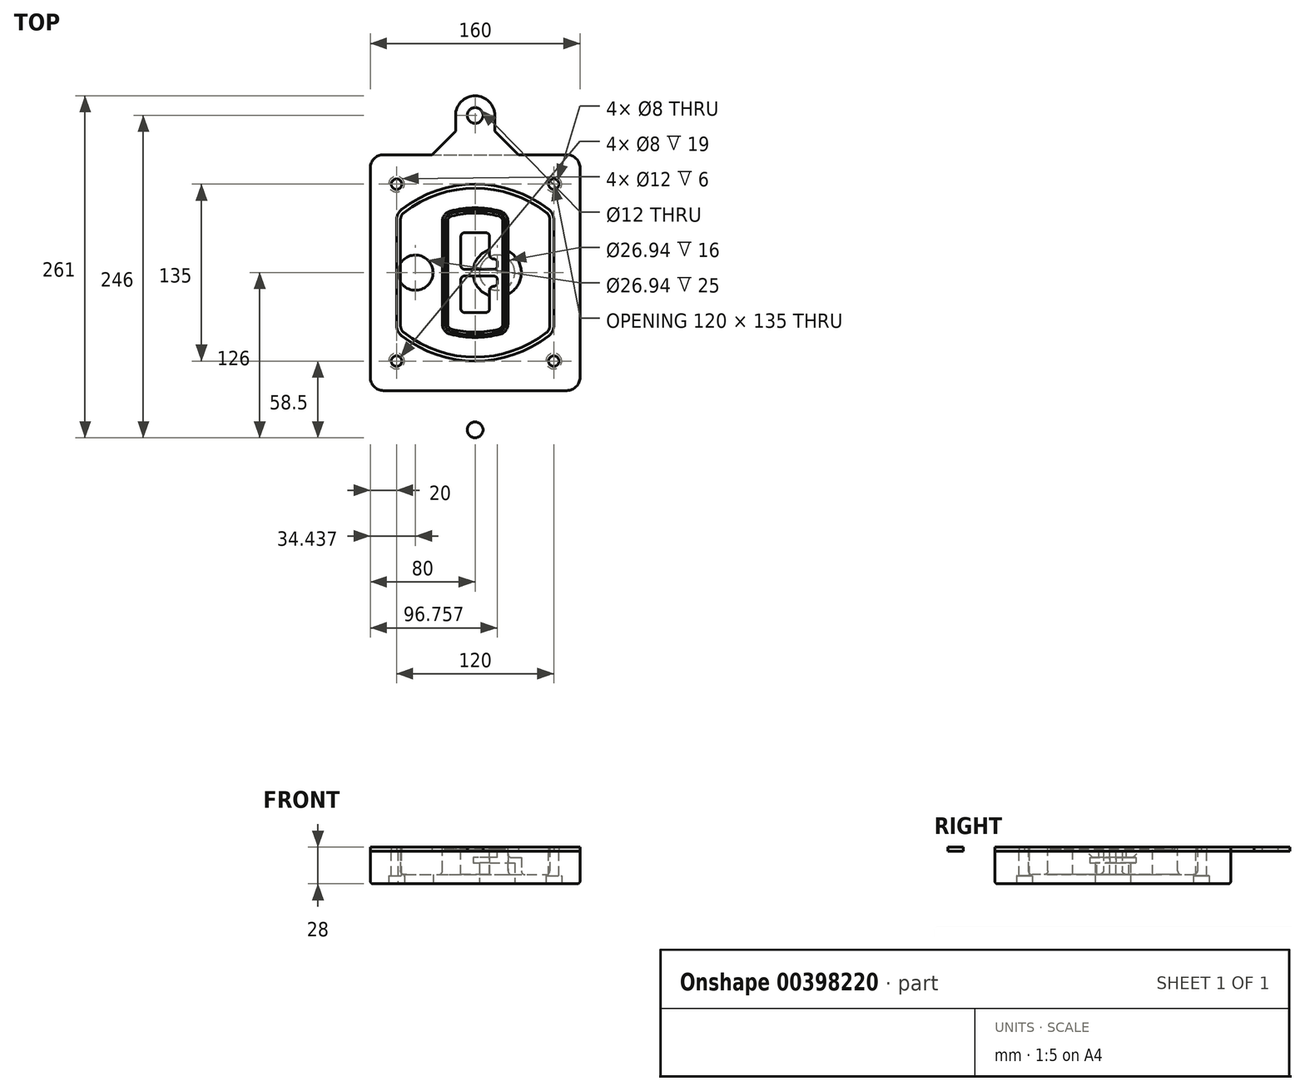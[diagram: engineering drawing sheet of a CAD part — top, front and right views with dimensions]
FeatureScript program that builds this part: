
annotation { "Feature Type Name" : "Feature", "Feature Type Description" : "" }
export const myFeature = defineFeature(function(context is Context, id is Id, definition is map)
    precondition{}
    {
        {
            var Q0;
            Q0=qCreatedBy(makeId("Top.planeOp"),FACE);
            var sketch = newSketch(context, id + "F0", { "sketchPlane" : qUnion([Q0])});
            skPoint(sketch, "E0.rect.middle", {"position": v(0, 0) * mm});
            skLineSegment(sketch, "E1.bottom", {"start": v(-70, -90) * mm, "end": v(70, -90) * mm});
            skLineSegment(sketch, "E1.top", {"start": v(-70, 90) * mm, "end": v(70, 90) * mm});
            skLineSegment(sketch, "E1.left", {"start": v(-80, -80) * mm, "end": v(-80, 80) * mm});
            skLineSegment(sketch, "E1.right", {"start": v(80, -80) * mm, "end": v(80, 80) * mm});
            skLineSegment(sketch, "E2", {"start": v(-80, 90) * mm, "end": v(80, -90) * mm, "construction": true});
            skLineSegment(sketch, "E3", {"start": v(80, 90) * mm, "end": v(-80, -90) * mm, "construction": true});
            skCircle(sketch, "E4", {"center": v(-60, 67.5) * mm, "radius": 4 * mm});
            skCircle(sketch, "E5", {"center": v(60, 67.5) * mm, "radius": 4 * mm});
            skCircle(sketch, "E6", {"center": v(60, -67.5) * mm, "radius": 4 * mm});
            skCircle(sketch, "E7", {"center": v(-60, -67.5) * mm, "radius": 4 * mm});
            skLineSegment(sketch, "E8", {"start": v(-60, 67.5) * mm, "end": v(60, 67.5) * mm, "construction": true});
            skLineSegment(sketch, "E9", {"start": v(60, 67.5) * mm, "end": v(60, -67.5) * mm, "construction": true});
            skLineSegment(sketch, "E10", {"start": v(60, -67.5) * mm, "end": v(-60, -67.5) * mm, "construction": true});
            skLineSegment(sketch, "E11", {"start": v(-60, -67.5) * mm, "end": v(-60, 67.5) * mm, "construction": true});
            skLineSegment(sketch, "E12", {"start": v(-60, 40.3) * mm, "end": v(-60, -40.3) * mm});
            skLineSegment(sketch, "E13", {"start": v(60, 40.3) * mm, "end": v(60, -40.3) * mm});
            skArc(sketch, "E14", {"start": v(56.15, 48.18) * mm, "mid": v(0, 67.5) * mm, "end": v(-56.15, 48.18) * mm});
            skArc(sketch, "E15", {"start": v(-56.15, -48.18) * mm, "mid": v(0, -67.5) * mm, "end": v(56.15, -48.18) * mm});
            skLineSegment(sketch, "E16", {"start": v(-60, 0) * mm, "end": v(60, 0) * mm, "construction": true});
            skPoint(sketch, "E17.visualSharp", {"position": v(-60, -45) * mm});
            skArc(sketch, "E17.filletArc", {"start": v(-60, -40.3) * mm, "mid": v(-58.99, -44.68) * mm, "end": v(-56.15, -48.18) * mm});
            skPoint(sketch, "E18.visualSharp", {"position": v(-60, 45) * mm});
            skArc(sketch, "E18.filletArc", {"start": v(-56.15, 48.18) * mm, "mid": v(-58.99, 44.68) * mm, "end": v(-60, 40.3) * mm});
            skPoint(sketch, "E19.visualSharp", {"position": v(60, 45) * mm});
            skArc(sketch, "E19.filletArc", {"start": v(60, 40.3) * mm, "mid": v(58.99, 44.68) * mm, "end": v(56.15, 48.18) * mm});
            skPoint(sketch, "E20.visualSharp", {"position": v(60, -45) * mm});
            skArc(sketch, "E20.filletArc", {"start": v(56.15, -48.18) * mm, "mid": v(58.99, -44.68) * mm, "end": v(60, -40.3) * mm});
            skPoint(sketch, "E21.visualSharp", {"position": v(-80, 90) * mm});
            skArc(sketch, "E21.filletArc", {"start": v(-70, 90) * mm, "mid": v(-77.07, 87.07) * mm, "end": v(-80, 80) * mm});
            skPoint(sketch, "E22.visualSharp", {"position": v(80, 90) * mm});
            skArc(sketch, "E22.filletArc", {"start": v(80, 80) * mm, "mid": v(77.07, 87.07) * mm, "end": v(70, 90) * mm});
            skPoint(sketch, "E23.visualSharp", {"position": v(80, -90) * mm});
            skArc(sketch, "E23.filletArc", {"start": v(70, -90) * mm, "mid": v(77.07, -87.07) * mm, "end": v(80, -80) * mm});
            skPoint(sketch, "E24.visualSharp", {"position": v(-80, -90) * mm});
            skArc(sketch, "E24.filletArc", {"start": v(-80, -80) * mm, "mid": v(-77.07, -87.07) * mm, "end": v(-70, -90) * mm});
            skArc(sketch, "E25.0", {"start": v(57, 40.3) * mm, "mid": v(56.3, 43.36) * mm, "end": v(54.3, 45.81) * mm});
            skLineSegment(sketch, "E25.1", {"start": v(57, 40.3) * mm, "end": v(57, -40.3) * mm});
            skArc(sketch, "E25.2", {"start": v(54.3, -45.81) * mm, "mid": v(56.3, -43.36) * mm, "end": v(57, -40.3) * mm});
            skArc(sketch, "E25.3", {"start": v(-54.3, -45.81) * mm, "mid": v(0, -64.5) * mm, "end": v(54.3, -45.81) * mm});
            skArc(sketch, "E25.4", {"start": v(-57, -40.3) * mm, "mid": v(-56.3, -43.36) * mm, "end": v(-54.3, -45.81) * mm});
            skArc(sketch, "E25.5", {"start": v(54.3, 45.81) * mm, "mid": v(0, 64.5) * mm, "end": v(-54.3, 45.81) * mm});
            skLineSegment(sketch, "E25.6", {"start": v(-57, 40.3) * mm, "end": v(-57, -40.3) * mm});
            skArc(sketch, "E25.7", {"start": v(-54.3, 45.81) * mm, "mid": v(-56.3, 43.36) * mm, "end": v(-57, 40.3) * mm});
            skArc(sketch, "E26.0", {"start": v(-58.62, 51.33) * mm, "mid": v(-62.58, 46.43) * mm, "end": v(-64, 40.3) * mm});
            skArc(sketch, "E26.1", {"start": v(58.62, 51.33) * mm, "mid": v(0, 71.5) * mm, "end": v(-58.62, 51.33) * mm});
            skArc(sketch, "E26.2", {"start": v(64, 40.3) * mm, "mid": v(62.58, 46.43) * mm, "end": v(58.62, 51.33) * mm});
            skLineSegment(sketch, "E26.3", {"start": v(64, 40.3) * mm, "end": v(64, -40.3) * mm});
            skArc(sketch, "E26.4", {"start": v(58.62, -51.33) * mm, "mid": v(62.58, -46.43) * mm, "end": v(64, -40.3) * mm});
            skLineSegment(sketch, "E26.5", {"start": v(-64, 40.3) * mm, "end": v(-64, -40.3) * mm});
            skArc(sketch, "E26.6", {"start": v(-58.62, -51.33) * mm, "mid": v(0, -71.5) * mm, "end": v(58.62, -51.33) * mm});
            skArc(sketch, "E26.7", {"start": v(-64, -40.3) * mm, "mid": v(-62.58, -46.43) * mm, "end": v(-58.62, -51.33) * mm});
            skSolve(sketch);
        }
        {
            var Q0;
            Q0=makeQuery(id+"F0.imprint","IMPRINT",FACE,{"disambiguationData":[TD([[makeQuery(id+"F0.imprint","IMPRINT",EDGE,{"derivedFrom":sQuery(id+"F0.wireOp",EDGE,"E1.bottom")}),1.0]])]});
            var Q1;
            Q1=makeQuery(id+"F0.imprint","IMPRINT",FACE,{"disambiguationData":[TD([[makeQuery(id+"F0.imprint","IMPRINT",EDGE,{"derivedFrom":sQuery(id+"F0.wireOp",EDGE,"E12")}),1.0]])]});
            var Q2;
            Q2=makeQuery(id+"F0.imprint","IMPRINT",FACE,{"disambiguationData":[TD([[makeQuery(id+"F0.imprint","IMPRINT",EDGE,{"derivedFrom":sQuery(id+"F0.wireOp",EDGE,"E25.0")}),1.0]])]});
            var Q3;
            Q3=makeQuery(id+"F0.imprint","IMPRINT",FACE,{"disambiguationData":[TD([[makeQuery(id+"F0.imprint","IMPRINT",EDGE,{"derivedFrom":sQuery(id+"F0.wireOp",EDGE,"E12")}),-1.0]])]});
            extrude(context, id + "F1", {"entities" : qUnion([Q0, Q1, Q2, Q3]), "oppositeDirection" : true, "depth" : 25 * mm});
        }
        {
            var Q0;
            Q0=makeQuery(id+"F0.imprint","IMPRINT",FACE,{"disambiguationData":[TD([[makeQuery(id+"F0.imprint","IMPRINT",EDGE,{"derivedFrom":sQuery(id+"F0.wireOp",EDGE,"E12")}),1.0]])]});
            extrude(context, id + "F2", {"entities" : qUnion([Q0]), "operationType" : NewBodyOperationType.ADD, "depth" : 3 * mm});
        }
        {
            var Q0;
            Q0=makeQuery(id+"F0.imprint","IMPRINT",FACE,{"disambiguationData":[TD([[makeQuery(id+"F0.imprint","IMPRINT",EDGE,{"derivedFrom":sQuery(id+"F0.wireOp",EDGE,"E25.0")}),1.0]])]});
            extrude(context, id + "F3", {"entities" : qUnion([Q0]), "operationType" : NewBodyOperationType.REMOVE, "oppositeDirection" : true, "depth" : 18 * mm});
        }
        {
            var Q0;
            Q0=makeQuery(id+"F2.opExtrude","CAP_FACE",FACE,{"disambiguationData":[OSD([sQuery(id+"F0.wireOp",EDGE,"E12"),sQuery(id+"F0.wireOp",EDGE,"E13"),sQuery(id+"F0.wireOp",EDGE,"E14"),sQuery(id+"F0.wireOp",EDGE,"E15"),sQuery(id+"F0.wireOp",EDGE,"E17.filletArc"),sQuery(id+"F0.wireOp",EDGE,"E18.filletArc"),sQuery(id+"F0.wireOp",EDGE,"E19.filletArc"),sQuery(id+"F0.wireOp",EDGE,"E20.filletArc"),sQuery(id+"F0.wireOp",EDGE,"E25.0"),sQuery(id+"F0.wireOp",EDGE,"E25.1"),sQuery(id+"F0.wireOp",EDGE,"E25.2"),sQuery(id+"F0.wireOp",EDGE,"E25.3"),sQuery(id+"F0.wireOp",EDGE,"E25.4"),sQuery(id+"F0.wireOp",EDGE,"E25.5"),sQuery(id+"F0.wireOp",EDGE,"E25.6"),sQuery(id+"F0.wireOp",EDGE,"E25.7")])],"isStart":false});
            var sketch = newSketch(context, id + "F4", { "sketchPlane" : qUnion([Q0])});
            skArc(sketch, "E27.0", {"start": v(-19.08, -46.97) * mm, "mid": v(0, -49.5) * mm, "end": v(19.08, -46.97) * mm});
            skArc(sketch, "E28.0", {"start": v(19.08, 46.97) * mm, "mid": v(0, 49.5) * mm, "end": v(-19.08, 46.97) * mm});
            skLineSegment(sketch, "E29", {"start": v(-25, 39.25) * mm, "end": v(-25, -39.25) * mm});
            skLineSegment(sketch, "E30", {"start": v(25, 39.25) * mm, "end": v(25, -39.25) * mm});
            skLineSegment(sketch, "E31", {"start": v(-25, 45.1) * mm, "end": v(25, 45.1) * mm, "construction": true});
            skLineSegment(sketch, "E32", {"start": v(-25, -45.1) * mm, "end": v(25, -45.1) * mm, "construction": true});
            skPoint(sketch, "E33.visualSharp", {"position": v(-25, 45.1) * mm});
            skArc(sketch, "E33.filletArc", {"start": v(-19.08, 46.97) * mm, "mid": v(-23.35, 44.11) * mm, "end": v(-25, 39.25) * mm});
            skPoint(sketch, "E34.visualSharp", {"position": v(25, 45.1) * mm});
            skArc(sketch, "E34.filletArc", {"start": v(25, 39.25) * mm, "mid": v(23.35, 44.11) * mm, "end": v(19.08, 46.97) * mm});
            skPoint(sketch, "E35.visualSharp", {"position": v(25, -45.1) * mm});
            skArc(sketch, "E35.filletArc", {"start": v(19.08, -46.97) * mm, "mid": v(23.35, -44.11) * mm, "end": v(25, -39.25) * mm});
            skPoint(sketch, "E36.visualSharp", {"position": v(-25, -45.1) * mm});
            skArc(sketch, "E36.filletArc", {"start": v(-25, -39.25) * mm, "mid": v(-23.35, -44.11) * mm, "end": v(-19.08, -46.97) * mm});
            skArc(sketch, "E37.0", {"start": v(54.3, 45.81) * mm, "mid": v(0, 64.5) * mm, "end": v(-54.3, 45.81) * mm});
            skArc(sketch, "E37.1", {"start": v(-54.3, 45.81) * mm, "mid": v(-56.3, 43.36) * mm, "end": v(-57, 40.3) * mm});
            skLineSegment(sketch, "E37.2", {"start": v(-57, 40.3) * mm, "end": v(-57, -40.3) * mm});
            skArc(sketch, "E37.3", {"start": v(-57, -40.3) * mm, "mid": v(-56.3, -43.36) * mm, "end": v(-54.3, -45.81) * mm});
            skArc(sketch, "E37.4", {"start": v(-54.3, -45.81) * mm, "mid": v(0, -64.5) * mm, "end": v(54.3, -45.81) * mm});
            skArc(sketch, "E37.5", {"start": v(54.3, -45.81) * mm, "mid": v(56.3, -43.36) * mm, "end": v(57, -40.3) * mm});
            skLineSegment(sketch, "E37.6", {"start": v(57, 40.3) * mm, "end": v(57, -40.3) * mm});
            skArc(sketch, "E37.7", {"start": v(57, 40.3) * mm, "mid": v(56.3, 43.36) * mm, "end": v(54.3, 45.81) * mm});
            skLineSegment(sketch, "E38.0", {"start": v(23, 39.25) * mm, "end": v(23, -39.25) * mm});
            skArc(sketch, "E38.1", {"start": v(18.56, -45.04) * mm, "mid": v(21.76, -42.9) * mm, "end": v(23, -39.25) * mm});
            skArc(sketch, "E38.2", {"start": v(-18.56, -45.04) * mm, "mid": v(0, -47.5) * mm, "end": v(18.56, -45.04) * mm});
            skArc(sketch, "E38.3", {"start": v(-23, -39.25) * mm, "mid": v(-21.76, -42.9) * mm, "end": v(-18.56, -45.04) * mm});
            skLineSegment(sketch, "E38.4", {"start": v(-23, 39.25) * mm, "end": v(-23, -39.25) * mm});
            skArc(sketch, "E38.5", {"start": v(23, 39.25) * mm, "mid": v(21.76, 42.9) * mm, "end": v(18.56, 45.04) * mm});
            skArc(sketch, "E38.6", {"start": v(-18.56, 45.04) * mm, "mid": v(-21.76, 42.9) * mm, "end": v(-23, 39.25) * mm});
            skArc(sketch, "E38.7", {"start": v(18.56, 45.04) * mm, "mid": v(0, 47.5) * mm, "end": v(-18.56, 45.04) * mm});
            skArc(sketch, "E39.0", {"start": v(21, 39.25) * mm, "mid": v(20.18, 41.68) * mm, "end": v(18.04, 43.1) * mm});
            skLineSegment(sketch, "E39.1", {"start": v(21, 39.25) * mm, "end": v(21, -39.25) * mm});
            skArc(sketch, "E39.2", {"start": v(18.04, -43.1) * mm, "mid": v(20.18, -41.68) * mm, "end": v(21, -39.25) * mm});
            skArc(sketch, "E39.3", {"start": v(-18.04, -43.1) * mm, "mid": v(0, -45.5) * mm, "end": v(18.04, -43.1) * mm});
            skArc(sketch, "E39.4", {"start": v(-21, -39.25) * mm, "mid": v(-20.18, -41.68) * mm, "end": v(-18.04, -43.1) * mm});
            skArc(sketch, "E39.5", {"start": v(18.04, 43.1) * mm, "mid": v(0, 45.5) * mm, "end": v(-18.04, 43.1) * mm});
            skLineSegment(sketch, "E39.6", {"start": v(-21, 39.25) * mm, "end": v(-21, -39.25) * mm});
            skArc(sketch, "E39.7", {"start": v(-18.04, 43.1) * mm, "mid": v(-20.18, 41.68) * mm, "end": v(-21, 39.25) * mm});
            skLineSegment(sketch, "E40", {"start": v(-25, 0) * mm, "end": v(25, 0) * mm, "construction": true});
            skLineSegment(sketch, "E41", {"start": v(-11, 5.5) * mm, "end": v(-11, 27.5) * mm});
            skLineSegment(sketch, "E42", {"start": v(-8, 30.5) * mm, "end": v(8, 30.5) * mm});
            skLineSegment(sketch, "E43", {"start": v(11, 27.5) * mm, "end": v(11, 13.5) * mm});
            skLineSegment(sketch, "E44", {"start": v(14, 10.5) * mm, "end": v(14, 10.5) * mm});
            skLineSegment(sketch, "E45", {"start": v(17, 7.5) * mm, "end": v(17, 5.5) * mm});
            skLineSegment(sketch, "E46", {"start": v(14, 2.5) * mm, "end": v(-8, 2.5) * mm});
            skPoint(sketch, "E47.visualSharp", {"position": v(-11, 30.5) * mm});
            skArc(sketch, "E47.filletArc", {"start": v(-8, 30.5) * mm, "mid": v(-10.12, 29.62) * mm, "end": v(-11, 27.5) * mm});
            skPoint(sketch, "E48.visualSharp", {"position": v(11, 30.5) * mm});
            skArc(sketch, "E48.filletArc", {"start": v(11, 27.5) * mm, "mid": v(10.12, 29.62) * mm, "end": v(8, 30.5) * mm});
            skPoint(sketch, "E49.visualSharp", {"position": v(11, 10.5) * mm});
            skArc(sketch, "E49.filletArc", {"start": v(11, 13.5) * mm, "mid": v(11.88, 11.38) * mm, "end": v(14, 10.5) * mm});
            skPoint(sketch, "E50.visualSharp", {"position": v(17, 10.5) * mm});
            skArc(sketch, "E50.filletArc", {"start": v(17, 7.5) * mm, "mid": v(16.12, 9.62) * mm, "end": v(14, 10.5) * mm});
            skPoint(sketch, "E51.visualSharp", {"position": v(17, 2.5) * mm});
            skArc(sketch, "E51.filletArc", {"start": v(14, 2.5) * mm, "mid": v(16.12, 3.38) * mm, "end": v(17, 5.5) * mm});
            skPoint(sketch, "E52.visualSharp", {"position": v(-11, 2.5) * mm});
            skArc(sketch, "E52.filletArc", {"start": v(-11, 5.5) * mm, "mid": v(-10.12, 3.38) * mm, "end": v(-8, 2.5) * mm});
            skLineSegment(sketch, "E53.0.MirrorCS", {"start": v(14, -2.5) * mm, "end": v(-8, -2.5) * mm});
            skArc(sketch, "E54.0.MirrorCS", {"start": v(-11, -5.5) * mm, "mid": v(-10.12, -3.38) * mm, "end": v(-8, -2.5) * mm});
            skLineSegment(sketch, "E55.0.MirrorCS", {"start": v(-11, -5.5) * mm, "end": v(-11, -27.5) * mm});
            skArc(sketch, "E56.0.MirrorCS", {"start": v(-8, -30.5) * mm, "mid": v(-10.12, -29.62) * mm, "end": v(-11, -27.5) * mm});
            skLineSegment(sketch, "E57.0.MirrorCS", {"start": v(-8, -30.5) * mm, "end": v(8, -30.5) * mm});
            skArc(sketch, "E58.0.MirrorCS", {"start": v(11, -27.5) * mm, "mid": v(10.12, -29.62) * mm, "end": v(8, -30.5) * mm});
            skLineSegment(sketch, "E59.0.MirrorCS", {"start": v(11, -27.5) * mm, "end": v(11, -13.5) * mm});
            skArc(sketch, "E60.0.MirrorCS", {"start": v(11, -13.5) * mm, "mid": v(11.88, -11.38) * mm, "end": v(14, -10.5) * mm});
            skArc(sketch, "E61.0.MirrorCS", {"start": v(17, -7.5) * mm, "mid": v(16.12, -9.62) * mm, "end": v(14, -10.5) * mm});
            skLineSegment(sketch, "E62.0.MirrorCS", {"start": v(17, -7.5) * mm, "end": v(17, -5.5) * mm});
            skArc(sketch, "E63.0.MirrorCS", {"start": v(14, -2.5) * mm, "mid": v(16.12, -3.38) * mm, "end": v(17, -5.5) * mm});
            skSolve(sketch);
        }
        {
            var Q0;
            Q0=makeQuery(id+"F4.imprint","IMPRINT",FACE,{"disambiguationData":[TD([[makeQuery(id+"F4.imprint","IMPRINT",EDGE,{"derivedFrom":sQuery(id+"F4.wireOp",EDGE,"E27.0")}),1.0]])]});
            var Q1;
            Q1=makeQuery(id+"F4.imprint","IMPRINT",FACE,{"disambiguationData":[TD([[makeQuery(id+"F4.imprint","IMPRINT",EDGE,{"derivedFrom":sQuery(id+"F4.wireOp",EDGE,"E38.0")}),-1.0]])]});
            var Q2;
            Q2=makeQuery(id+"F4.imprint","IMPRINT",FACE,{"disambiguationData":[TD([[makeQuery(id+"F4.imprint","IMPRINT",EDGE,{"derivedFrom":sQuery(id+"F4.wireOp",EDGE,"E39.0")}),1.0]])]});
            extrude(context, id + "F5", {"entities" : qUnion([Q0, Q1, Q2]), "operationType" : NewBodyOperationType.ADD, "endBound" : BoundingType.UP_TO_NEXT, "oppositeDirection" : true, "depth" : 25 * mm});
        }
        {
            var Q0;
            Q0=makeQuery(id+"F4.imprint","IMPRINT",FACE,{"disambiguationData":[TD([[makeQuery(id+"F4.imprint","IMPRINT",EDGE,{"derivedFrom":sQuery(id+"F4.wireOp",EDGE,"E38.0")}),-1.0]])]});
            extrude(context, id + "F6", {"entities" : qUnion([Q0]), "operationType" : NewBodyOperationType.REMOVE, "oppositeDirection" : true, "depth" : 2 * mm});
        }
        {
            var Q0;
            Q0=makeQuery(id+"F1.opExtrude","CAP_FACE",FACE,{"disambiguationData":[OSD([sQuery(id+"F0.wireOp",EDGE,"E1.bottom"),sQuery(id+"F0.wireOp",EDGE,"E1.top"),sQuery(id+"F0.wireOp",EDGE,"E1.left"),sQuery(id+"F0.wireOp",EDGE,"E1.right"),sQuery(id+"F0.wireOp",EDGE,"E4"),sQuery(id+"F0.wireOp",EDGE,"E5"),sQuery(id+"F0.wireOp",EDGE,"E6"),sQuery(id+"F0.wireOp",EDGE,"E7"),sQuery(id+"F0.wireOp",EDGE,"E21.filletArc"),sQuery(id+"F0.wireOp",EDGE,"E22.filletArc"),sQuery(id+"F0.wireOp",EDGE,"E23.filletArc"),sQuery(id+"F0.wireOp",EDGE,"E24.filletArc")])],"isStart":false});
            var sketch = newSketch(context, id + "F7", { "sketchPlane" : qUnion([Q0])});
            skCircle(sketch, "E64", {"center": v(16.76, 0) * mm, "radius": 13.47 * mm});
            skCircle(sketch, "E65", {"center": v(-45.56, 0) * mm, "radius": 13.47 * mm});
            skLineSegment(sketch, "E66", {"start": v(80, 0) * mm, "end": v(-80, 0) * mm});
            skCircle(sketch, "E67", {"center": v(16.76, 0) * mm, "radius": 18.47 * mm});
            skCircle(sketch, "E68", {"center": v(60, -67.5) * mm, "radius": 6 * mm});
            skCircle(sketch, "E69", {"center": v(-60, -67.5) * mm, "radius": 6 * mm});
            skCircle(sketch, "E70", {"center": v(-60, 67.5) * mm, "radius": 6 * mm});
            skCircle(sketch, "E71", {"center": v(60, 67.5) * mm, "radius": 6 * mm});
            skSolve(sketch);
        }
        {
            var Q0;
            {var subQ1=sQuery(id+"F7.wireOp",EDGE,"E66");var subQ4=sQuery(id+"F7.wireOp",EDGE,"E64");var subQ6=makeQuery(id+"F7.imprint","INTERSECT",VERTEX,{"disambiguationData":[OD(0.0)],"derivedFrom":[subQ4,subQ1]});Q0=makeQuery(id+"F7.imprint","IMPRINT",FACE,{"disambiguationData":[TD([[makeQuery(id+"F7.imprint","IMPRINT",EDGE,{"disambiguationData":[TD([[subQ6,-1.0]])],"derivedFrom":subQ4}),-1.0]])]});}
            var Q1;
            {var subQ0=sQuery(id+"F7.wireOp",EDGE,"E66");var subQ1=sQuery(id+"F7.wireOp",EDGE,"E64");var subQ3=makeQuery(id+"F7.imprint","INTERSECT",VERTEX,{"disambiguationData":[OD(0.0)],"derivedFrom":[subQ1,subQ0]});Q1=makeQuery(id+"F7.imprint","IMPRINT",FACE,{"disambiguationData":[TD([[makeQuery(id+"F7.imprint","IMPRINT",EDGE,{"disambiguationData":[TD([[subQ3,-1.0]])],"derivedFrom":subQ1}),1.0]])]});}
            var Q2;
            {var subQ0=sQuery(id+"F7.wireOp",EDGE,"E66");var subQ1=sQuery(id+"F7.wireOp",EDGE,"E64");var subQ3=makeQuery(id+"F7.imprint","INTERSECT",VERTEX,{"disambiguationData":[OD(0.0)],"derivedFrom":[subQ1,subQ0]});Q2=makeQuery(id+"F7.imprint","IMPRINT",FACE,{"disambiguationData":[TD([[makeQuery(id+"F7.imprint","IMPRINT",EDGE,{"disambiguationData":[TD([[subQ3,1.0]])],"derivedFrom":subQ1}),1.0]])]});}
            var Q3;
            {var subQ1=sQuery(id+"F7.wireOp",EDGE,"E66");var subQ4=sQuery(id+"F7.wireOp",EDGE,"E64");var subQ6=makeQuery(id+"F7.imprint","INTERSECT",VERTEX,{"disambiguationData":[OD(0.0)],"derivedFrom":[subQ4,subQ1]});Q3=makeQuery(id+"F7.imprint","IMPRINT",FACE,{"disambiguationData":[TD([[makeQuery(id+"F7.imprint","IMPRINT",EDGE,{"disambiguationData":[TD([[subQ6,1.0]])],"derivedFrom":subQ4}),-1.0]])]});}
            extrude(context, id + "F8", {"entities" : qUnion([Q0, Q1, Q2, Q3]), "operationType" : NewBodyOperationType.ADD, "oppositeDirection" : true, "depth" : 20 * mm});
        }
        {
            var Q0;
            {var subQ0=sQuery(id+"F7.wireOp",EDGE,"E66");var subQ1=sQuery(id+"F7.wireOp",EDGE,"E64");var subQ3=makeQuery(id+"F7.imprint","INTERSECT",VERTEX,{"disambiguationData":[OD(0.0)],"derivedFrom":[subQ1,subQ0]});Q0=makeQuery(id+"F7.imprint","IMPRINT",FACE,{"disambiguationData":[TD([[makeQuery(id+"F7.imprint","IMPRINT",EDGE,{"disambiguationData":[TD([[subQ3,-1.0]])],"derivedFrom":subQ1}),1.0]])]});}
            var Q1;
            {var subQ0=sQuery(id+"F7.wireOp",EDGE,"E66");var subQ1=sQuery(id+"F7.wireOp",EDGE,"E64");var subQ3=makeQuery(id+"F7.imprint","INTERSECT",VERTEX,{"disambiguationData":[OD(0.0)],"derivedFrom":[subQ1,subQ0]});Q1=makeQuery(id+"F7.imprint","IMPRINT",FACE,{"disambiguationData":[TD([[makeQuery(id+"F7.imprint","IMPRINT",EDGE,{"disambiguationData":[TD([[subQ3,1.0]])],"derivedFrom":subQ1}),1.0]])]});}
            extrude(context, id + "F9", {"entities" : qUnion([Q0, Q1]), "operationType" : NewBodyOperationType.REMOVE, "oppositeDirection" : true, "depth" : 16 * mm});
        }
        {
            var Q0;
            {var subQ0=sQuery(id+"F7.wireOp",EDGE,"E66");var subQ1=sQuery(id+"F7.wireOp",EDGE,"E65");var subQ3=makeQuery(id+"F7.imprint","INTERSECT",VERTEX,{"disambiguationData":[OD(0.0)],"derivedFrom":[subQ1,subQ0]});Q0=makeQuery(id+"F7.imprint","IMPRINT",FACE,{"disambiguationData":[TD([[makeQuery(id+"F7.imprint","IMPRINT",EDGE,{"disambiguationData":[TD([[subQ3,-1.0]])],"derivedFrom":subQ1}),1.0]])]});}
            var Q1;
            {var subQ0=sQuery(id+"F7.wireOp",EDGE,"E66");var subQ1=sQuery(id+"F7.wireOp",EDGE,"E65");var subQ3=makeQuery(id+"F7.imprint","INTERSECT",VERTEX,{"disambiguationData":[OD(0.0)],"derivedFrom":[subQ1,subQ0]});Q1=makeQuery(id+"F7.imprint","IMPRINT",FACE,{"disambiguationData":[TD([[makeQuery(id+"F7.imprint","IMPRINT",EDGE,{"disambiguationData":[TD([[subQ3,1.0]])],"derivedFrom":subQ1}),1.0]])]});}
            extrude(context, id + "F10", {"entities" : qUnion([Q0, Q1]), "operationType" : NewBodyOperationType.REMOVE, "oppositeDirection" : true, "depth" : 25 * mm});
        }
        {
            var Q0;
            Q0=makeQuery(id+"F7.imprint","IMPRINT",FACE,{"disambiguationData":[TD([[makeQuery(id+"F7.imprint","IMPRINT",EDGE,{"derivedFrom":sQuery(id+"F7.wireOp",EDGE,"E68")}),1.0]])]});
            var Q1;
            Q1=makeQuery(id+"F7.imprint","IMPRINT",FACE,{"disambiguationData":[TD([[makeQuery(id+"F7.imprint","IMPRINT",EDGE,{"derivedFrom":makeQuery(id+"F1.opExtrude","CAP_EDGE",EDGE,{"disambiguationData":[OSD([sQuery(id+"F0.wireOp",EDGE,"E5")])],"isStart":false})}),-1.0]])]});
            var Q2;
            Q2=makeQuery(id+"F7.imprint","IMPRINT",FACE,{"disambiguationData":[TD([[makeQuery(id+"F7.imprint","IMPRINT",EDGE,{"derivedFrom":sQuery(id+"F7.wireOp",EDGE,"E69")}),1.0]])]});
            var Q3;
            Q3=makeQuery(id+"F7.imprint","IMPRINT",FACE,{"disambiguationData":[TD([[makeQuery(id+"F7.imprint","IMPRINT",EDGE,{"derivedFrom":makeQuery(id+"F1.opExtrude","CAP_EDGE",EDGE,{"disambiguationData":[OSD([sQuery(id+"F0.wireOp",EDGE,"E4")])],"isStart":false})}),-1.0]])]});
            var Q4;
            Q4=makeQuery(id+"F7.imprint","IMPRINT",FACE,{"disambiguationData":[TD([[makeQuery(id+"F7.imprint","IMPRINT",EDGE,{"derivedFrom":sQuery(id+"F7.wireOp",EDGE,"E70")}),1.0]])]});
            var Q5;
            Q5=makeQuery(id+"F7.imprint","IMPRINT",FACE,{"disambiguationData":[TD([[makeQuery(id+"F7.imprint","IMPRINT",EDGE,{"derivedFrom":makeQuery(id+"F1.opExtrude","CAP_EDGE",EDGE,{"disambiguationData":[OSD([sQuery(id+"F0.wireOp",EDGE,"E7")])],"isStart":false})}),-1.0]])]});
            var Q6;
            Q6=makeQuery(id+"F7.imprint","IMPRINT",FACE,{"disambiguationData":[TD([[makeQuery(id+"F7.imprint","IMPRINT",EDGE,{"derivedFrom":sQuery(id+"F7.wireOp",EDGE,"E71")}),1.0]])]});
            var Q7;
            Q7=makeQuery(id+"F7.imprint","IMPRINT",FACE,{"disambiguationData":[TD([[makeQuery(id+"F7.imprint","IMPRINT",EDGE,{"derivedFrom":makeQuery(id+"F1.opExtrude","CAP_EDGE",EDGE,{"disambiguationData":[OSD([sQuery(id+"F0.wireOp",EDGE,"E6")])],"isStart":false})}),-1.0]])]});
            extrude(context, id + "F11", {"entities" : qUnion([Q0, Q1, Q2, Q3, Q4, Q5, Q6, Q7]), "operationType" : NewBodyOperationType.REMOVE, "oppositeDirection" : true, "depth" : 6 * mm});
        }
        {
            var Q0;
            Q0=makeQuery(id+"F9.boolean.opBoolean","COPY",FACE,{"derivedFrom":makeQuery(id+"F9.opExtrude","CAP_FACE",FACE,{"disambiguationData":[OSD([sQuery(id+"F7.wireOp",EDGE,"E64")])],"isStart":false})});
            var sketch = newSketch(context, id + "F12", { "sketchPlane" : qUnion([Q0])});
            skArc(sketch, "E72.0", {"start": v(11, 17.55) * mm, "mid": v(2.57, 11.82) * mm, "end": v(-1.54, 2.5) * mm});
            skArc(sketch, "E72.1", {"start": v(-1.54, -2.5) * mm, "mid": v(2.57, -11.82) * mm, "end": v(11, -17.55) * mm});
            skLineSegment(sketch, "E73", {"start": v(-1.54, -2.5) * mm, "end": v(14, -2.5) * mm});
            skLineSegment(sketch, "E74.0", {"start": v(14, 2.5) * mm, "end": v(-1.54, 2.5) * mm});
            skArc(sketch, "E74.1", {"start": v(14, 2.5) * mm, "mid": v(16.12, 3.38) * mm, "end": v(17, 5.5) * mm});
            skLineSegment(sketch, "E74.2", {"start": v(17, 7.5) * mm, "end": v(17, 5.5) * mm});
            skArc(sketch, "E74.3", {"start": v(17, 7.5) * mm, "mid": v(16.12, 9.62) * mm, "end": v(14, 10.5) * mm});
            skArc(sketch, "E74.4", {"start": v(11, 13.5) * mm, "mid": v(11.88, 11.38) * mm, "end": v(14, 10.5) * mm});
            skLineSegment(sketch, "E74.5", {"start": v(11, 17.55) * mm, "end": v(11, 13.5) * mm});
            skLineSegment(sketch, "E74.7", {"start": v(14, -2.5) * mm, "end": v(-1.54, -2.5) * mm});
            skArc(sketch, "E74.8", {"start": v(14, -2.5) * mm, "mid": v(16.12, -3.38) * mm, "end": v(17, -5.5) * mm});
            skLineSegment(sketch, "E74.9", {"start": v(17, -7.5) * mm, "end": v(17, -5.5) * mm});
            skArc(sketch, "E74.10", {"start": v(17, -7.5) * mm, "mid": v(16.12, -9.62) * mm, "end": v(14, -10.5) * mm});
            skArc(sketch, "E74.11", {"start": v(11, -13.5) * mm, "mid": v(11.88, -11.38) * mm, "end": v(14, -10.5) * mm});
            skLineSegment(sketch, "E74.12", {"start": v(11, -17.55) * mm, "end": v(11, -13.5) * mm});
            skPoint(sketch, "E75.orphan", {"position": v(11, -27.5) * mm});
            skPoint(sketch, "E76.orphan", {"position": v(-8, -2.5) * mm});
            skPoint(sketch, "E77.orphan", {"position": v(-8, 2.5) * mm});
            skPoint(sketch, "E78.orphan", {"position": v(11, 27.5) * mm});
            skSolve(sketch);
        }
        {
            var Q0;
            {var subQ7=sQuery(id+"F12.wireOp",EDGE,"E72.0");var subQ14=sQuery(id+"F12.wireOp",EDGE,"E72.1");var subQ16=sQuery(id+"F12.wireOp",EDGE,"E74.1");var subQ18=sQuery(id+"F12.wireOp",EDGE,"E74.8");Q0=qUnion([makeQuery(id+"F12.imprint","IMPRINT",FACE,{"disambiguationData":[TD([[makeQuery(id+"F12.imprint","IMPRINT",EDGE,{"derivedFrom":subQ7}),1.0]])]}),makeQuery(id+"F12.imprint","IMPRINT",FACE,{"disambiguationData":[TD([[makeQuery(id+"F12.imprint","IMPRINT",EDGE,{"derivedFrom":subQ14}),1.0]])]}),makeQuery(id+"F12.imprint","IMPRINT",FACE,{"disambiguationData":[TD([[makeQuery(id+"F12.imprint","IMPRINT",EDGE,{"derivedFrom":subQ16}),1.0]])]}),makeQuery(id+"F12.imprint","IMPRINT",FACE,{"disambiguationData":[TD([[makeQuery(id+"F12.imprint","IMPRINT",EDGE,{"derivedFrom":subQ18}),-1.0]])]})]);}
            var Q1;
            Q1=makeQuery(id+"F5.boolean.opBoolean","SPLIT",FACE,{"disambiguationData":[TD([makeQuery(id+"F5.opExtrude","SWEPT_FACE",FACE,{"disambiguationData":[OSD([sQuery(id+"F4.wireOp",EDGE,"E41")])]})])],"derivedFrom":makeQuery(id+"F3.boolean.opBoolean","COPY",FACE,{"derivedFrom":makeQuery(id+"F3.opExtrude","CAP_FACE",FACE,{"disambiguationData":[OSD([sQuery(id+"F0.wireOp",EDGE,"E25.0"),sQuery(id+"F0.wireOp",EDGE,"E25.1"),sQuery(id+"F0.wireOp",EDGE,"E25.2"),sQuery(id+"F0.wireOp",EDGE,"E25.3"),sQuery(id+"F0.wireOp",EDGE,"E25.4"),sQuery(id+"F0.wireOp",EDGE,"E25.5"),sQuery(id+"F0.wireOp",EDGE,"E25.6"),sQuery(id+"F0.wireOp",EDGE,"E25.7")])],"isStart":false})})});
            extrude(context, id + "F13", {"entities" : qUnion([Q0]), "operationType" : NewBodyOperationType.REMOVE, "endBound" : BoundingType.UP_TO_SURFACE, "endBoundEntityFace" : qUnion([Q1]), "depth" : 25 * mm});
        }
        {
            var Q0;
            Q0=makeQuery(id+"F3.boolean.opBoolean","COPY",EDGE,{"derivedFrom":makeQuery(id+"F3.opExtrude","CAP_EDGE",EDGE,{"disambiguationData":[OSD([sQuery(id+"F0.wireOp",EDGE,"E25.6")])],"isStart":false})});
            var Q1;
            Q1=makeQuery(id+"F8.boolean.opBoolean","INTERSECT",EDGE,{"derivedFrom":[makeQuery(id+"F5.opExtrude","SWEPT_FACE",FACE,{"disambiguationData":[OSD([sQuery(id+"F4.wireOp",EDGE,"E30")])]}),makeQuery(id+"F8.opExtrude","CAP_FACE",FACE,{"disambiguationData":[OSD([sQuery(id+"F7.wireOp",EDGE,"E67")])],"isStart":false})]});
            var Q2;
            Q2=makeQuery(id+"F8.boolean.opBoolean","INTERSECT",EDGE,{"disambiguationData":[OD(1.0)],"derivedFrom":[makeQuery(id+"F5.opExtrude","SWEPT_FACE",FACE,{"disambiguationData":[OSD([sQuery(id+"F4.wireOp",EDGE,"E30")])]}),makeQuery(id+"F8.opExtrude","SWEPT_FACE",FACE,{"disambiguationData":[OSD([sQuery(id+"F7.wireOp",EDGE,"E67")])]})]});
            var Q3;
            {var subQ0=sQuery(id+"F4.wireOp",EDGE,"E30");Q3=makeQuery(id+"F8.boolean.opBoolean","SPLIT",EDGE,{"disambiguationData":[TD([makeQuery(id+"F5.opExtrude","SWEPT_FACE",FACE,{"disambiguationData":[OSD([sQuery(id+"F4.wireOp",EDGE,"E35.filletArc")])]})])],"derivedFrom":makeQuery(id+"F5.opExtrude","CAP_EDGE",EDGE,{"disambiguationData":[OSD([subQ0])],"isStart":false})});}
            var Q4;
            {var subQ0=sQuery(id+"F0.wireOp",EDGE,"E25.7");var subQ1=sQuery(id+"F0.wireOp",EDGE,"E25.1");var subQ2=sQuery(id+"F0.wireOp",EDGE,"E25.6");var subQ3=sQuery(id+"F0.wireOp",EDGE,"E25.5");var subQ4=sQuery(id+"F0.wireOp",EDGE,"E25.4");var subQ5=sQuery(id+"F0.wireOp",EDGE,"E25.0");var subQ6=sQuery(id+"F0.wireOp",EDGE,"E25.2");var subQ7=sQuery(id+"F0.wireOp",EDGE,"E25.3");Q4=makeQuery(id+"F8.boolean.opBoolean","INTERSECT",EDGE,{"derivedFrom":[makeQuery(id+"F5.boolean.opBoolean","SPLIT",FACE,{"disambiguationData":[TD([makeQuery(id+"F2.opExtrude","SWEPT_FACE",FACE,{"disambiguationData":[OSD([subQ5])]})])],"derivedFrom":makeQuery(id+"F3.boolean.opBoolean","COPY",FACE,{"derivedFrom":makeQuery(id+"F3.opExtrude","CAP_FACE",FACE,{"disambiguationData":[OSD([subQ5,subQ1,subQ6,subQ7,subQ4,subQ3,subQ2,subQ0])],"isStart":false})})}),makeQuery(id+"F8.opExtrude","SWEPT_FACE",FACE,{"disambiguationData":[OSD([sQuery(id+"F7.wireOp",EDGE,"E67")])]})]});}
            var Q5;
            Q5=makeQuery(id+"F8.boolean.opBoolean","INTERSECT",EDGE,{"disambiguationData":[OD(0.0)],"derivedFrom":[makeQuery(id+"F5.opExtrude","SWEPT_FACE",FACE,{"disambiguationData":[OSD([sQuery(id+"F4.wireOp",EDGE,"E30")])]}),makeQuery(id+"F8.opExtrude","SWEPT_FACE",FACE,{"disambiguationData":[OSD([sQuery(id+"F7.wireOp",EDGE,"E67")])]})]});
            fillet(context, id + "F14", {"entities" : qUnion([Q0, Q1, Q2, Q3, Q4, Q5]), "radius" : 3 * mm, "tangentPropagation" : true, "allowEdgeOverflow" : false});
        }
        {
            var Q0;
            Q0=makeQuery(id+"F1.opExtrude","CAP_EDGE",EDGE,{"disambiguationData":[OSD([sQuery(id+"F0.wireOp",EDGE,"E1.bottom")])],"isStart":false});
            fillet(context, id + "F15", {"entities" : qUnion([Q0]), "radius" : 2 * mm, "tangentPropagation" : true, "allowEdgeOverflow" : false});
        }
        {
            var Q0;
            {var subQ0=sQuery(id+"F0.wireOp",EDGE,"E21.filletArc");var subQ1=sQuery(id+"F0.wireOp",EDGE,"E7");var subQ2=sQuery(id+"F0.wireOp",EDGE,"E6");var subQ3=sQuery(id+"F0.wireOp",EDGE,"E5");var subQ4=sQuery(id+"F0.wireOp",EDGE,"E4");var subQ5=sQuery(id+"F0.wireOp",EDGE,"E22.filletArc");var subQ6=sQuery(id+"F0.wireOp",EDGE,"E1.bottom");var subQ7=sQuery(id+"F0.wireOp",EDGE,"E1.right");var subQ8=sQuery(id+"F0.wireOp",EDGE,"E1.top");var subQ9=sQuery(id+"F0.wireOp",EDGE,"E1.left");var subQ10=sQuery(id+"F0.wireOp",EDGE,"E23.filletArc");var subQ11=sQuery(id+"F0.wireOp",EDGE,"E24.filletArc");Q0=makeQuery(id+"F2.boolean.opBoolean","SPLIT",FACE,{"disambiguationData":[TD([makeQuery(id+"F1.opExtrude","SWEPT_FACE",FACE,{"disambiguationData":[OSD([subQ6])]})])],"derivedFrom":makeQuery(id+"F1.opExtrude","CAP_FACE",FACE,{"disambiguationData":[OSD([subQ6,subQ8,subQ9,subQ7,subQ4,subQ3,subQ2,subQ1,subQ0,subQ5,subQ10,subQ11])],"isStart":true})});}
            var sketch = newSketch(context, id + "F16", { "sketchPlane" : qUnion([Q0])});
            skLineSegment(sketch, "E79.0", {"start": v(-70, -90) * mm, "end": v(70, -90) * mm});
            skArc(sketch, "E80.1", {"start": v(-80, -80) * mm, "mid": v(-77.07, -87.07) * mm, "end": v(-70, -90) * mm});
            skLineSegment(sketch, "E81.0", {"start": v(-80, -80) * mm, "end": v(-80, 80) * mm});
            skArc(sketch, "E82.0", {"start": v(-70, 90) * mm, "mid": v(-77.07, 87.07) * mm, "end": v(-80, 80) * mm});
            skLineSegment(sketch, "E83.0", {"start": v(-70, 90) * mm, "end": v(70, 90) * mm});
            skArc(sketch, "E84.0", {"start": v(80, 80) * mm, "mid": v(77.07, 87.07) * mm, "end": v(70, 90) * mm});
            skLineSegment(sketch, "E85.0", {"start": v(80, -80) * mm, "end": v(80, 80) * mm});
            skArc(sketch, "E86.0", {"start": v(70, -90) * mm, "mid": v(77.07, -87.07) * mm, "end": v(80, -80) * mm});
            skLineSegment(sketch, "E87.0", {"start": v(60, 40.3) * mm, "end": v(60, -40.3) * mm});
            skArc(sketch, "E88.0", {"start": v(60, 40.3) * mm, "mid": v(58.99, 44.68) * mm, "end": v(56.15, 48.18) * mm});
            skArc(sketch, "E89.0", {"start": v(56.15, 48.18) * mm, "mid": v(0, 67.5) * mm, "end": v(-56.15, 48.18) * mm});
            skArc(sketch, "E90.0", {"start": v(-56.15, 48.18) * mm, "mid": v(-58.99, 44.68) * mm, "end": v(-60, 40.3) * mm});
            skLineSegment(sketch, "E91.0", {"start": v(-60, 40.3) * mm, "end": v(-60, -40.3) * mm});
            skArc(sketch, "E92.0", {"start": v(-60, -40.3) * mm, "mid": v(-58.99, -44.68) * mm, "end": v(-56.15, -48.18) * mm});
            skArc(sketch, "E93.0", {"start": v(-56.15, -48.18) * mm, "mid": v(0, -67.5) * mm, "end": v(56.15, -48.18) * mm});
            skCircle(sketch, "E94.0", {"center": v(-60, 67.5) * mm, "radius": 4 * mm});
            skCircle(sketch, "E95.0", {"center": v(60, 67.5) * mm, "radius": 4 * mm});
            skCircle(sketch, "E96.0", {"center": v(60, -67.5) * mm, "radius": 4 * mm});
            skCircle(sketch, "E97.0", {"center": v(-60, -67.5) * mm, "radius": 4 * mm});
            skCircle(sketch, "E98", {"center": v(0, 120) * mm, "radius": 6 * mm});
            skLineSegment(sketch, "E99", {"start": v(0, 120) * mm, "end": v(0, 90) * mm, "construction": true});
            skArc(sketch, "E100", {"start": v(15, 120) * mm, "mid": v(0, 135) * mm, "end": v(-15, 120) * mm});
            skLineSegment(sketch, "E101", {"start": v(-15, 120) * mm, "end": v(-15, 108) * mm});
            skLineSegment(sketch, "E102", {"start": v(15, 120) * mm, "end": v(15, 108) * mm});
            skLineSegment(sketch, "E103", {"start": v(-15, 108) * mm, "end": v(-33, 90) * mm});
            skPoint(sketch, "E104", {"position": v(0, 90) * mm});
            skPoint(sketch, "E105", {"position": v(33, 90) * mm});
            skLineSegment(sketch, "E106", {"start": v(15, 108) * mm, "end": v(33, 90) * mm});
            skLineSegment(sketch, "E107", {"start": v(-80, 0) * mm, "end": v(80, 0) * mm, "construction": true});
            skPoint(sketch, "E108.MirrorP", {"position": v(0, -90) * mm});
            skLineSegment(sketch, "E109.MirrorCS", {"start": v(0, -120) * mm, "end": v(0, -90) * mm});
            skLineSegment(sketch, "E110.MirrorCS", {"start": v(-15, -108) * mm, "end": v(-33, -90) * mm});
            skLineSegment(sketch, "E111.MirrorCS", {"start": v(15, -120) * mm, "end": v(15, -108) * mm});
            skPoint(sketch, "E112.MirrorP", {"position": v(33, -90) * mm});
            skArc(sketch, "E113.MirrorCS", {"start": v(15, -120) * mm, "mid": v(0, -135) * mm, "end": v(-15, -120) * mm});
            skLineSegment(sketch, "E114.MirrorCS", {"start": v(15, -108) * mm, "end": v(33, -90) * mm});
            skCircle(sketch, "E115.MirrorC", {"center": v(0, -120) * mm, "radius": 6 * mm});
            skLineSegment(sketch, "E116.MirrorCS", {"start": v(-15, -120) * mm, "end": v(-15, -108) * mm});
            skLineSegment(sketch, "E117.MirrorCS", {"start": v(0, -120) * mm, "end": v(0, -90) * mm, "construction": true});
            skArc(sketch, "E118.MirrorCS", {"start": v(80, -80) * mm, "mid": v(77.07, -87.07) * mm, "end": v(70, -90) * mm});
            skSolve(sketch);
        }
        {
            var Q0;
            {var subQ6=sQuery(id+"F16.wireOp",EDGE,"E80.1");Q0=makeQuery(id+"F16.imprint","IMPRINT",FACE,{"disambiguationData":[TD([[makeQuery(id+"F16.imprint","IMPRINT",EDGE,{"derivedFrom":subQ6}),1.0]])]});}
            var Q1;
            Q1=makeQuery(id+"F16.imprint","IMPRINT",FACE,{"disambiguationData":[TD([[makeQuery(id+"F16.imprint","IMPRINT",EDGE,{"derivedFrom":sQuery(id+"F16.wireOp",EDGE,"E98")}),-1.0]])]});
            var Q2;
            Q2=makeQuery(id+"F16.imprint","IMPRINT",FACE,{"disambiguationData":[TD([[makeQuery(id+"F16.imprint","IMPRINT",EDGE,{"derivedFrom":sQuery(id+"F16.wireOp",EDGE,"E115.MirrorC")}),1.0]])]});
            var Q3;
            Q3=sQuery(id+"F16.wireOp",EDGE,"E117.MirrorCS");
            var Q4;
            Q4=makeQuery(id+"F2.opExtrude","CAP_FACE",FACE,{"disambiguationData":[OSD([sQuery(id+"F0.wireOp",EDGE,"E12"),sQuery(id+"F0.wireOp",EDGE,"E13"),sQuery(id+"F0.wireOp",EDGE,"E14"),sQuery(id+"F0.wireOp",EDGE,"E15"),sQuery(id+"F0.wireOp",EDGE,"E17.filletArc"),sQuery(id+"F0.wireOp",EDGE,"E18.filletArc"),sQuery(id+"F0.wireOp",EDGE,"E19.filletArc"),sQuery(id+"F0.wireOp",EDGE,"E20.filletArc"),sQuery(id+"F0.wireOp",EDGE,"E25.0"),sQuery(id+"F0.wireOp",EDGE,"E25.1"),sQuery(id+"F0.wireOp",EDGE,"E25.2"),sQuery(id+"F0.wireOp",EDGE,"E25.3"),sQuery(id+"F0.wireOp",EDGE,"E25.4"),sQuery(id+"F0.wireOp",EDGE,"E25.5"),sQuery(id+"F0.wireOp",EDGE,"E25.6"),sQuery(id+"F0.wireOp",EDGE,"E25.7")])],"isStart":false});
            extrude(context, id + "F17", {"entities" : qUnion([Q0, Q1, Q2]), "surfaceEntities" : qUnion([Q3]), "endBound" : BoundingType.UP_TO_SURFACE, "endBoundEntityFace" : qUnion([Q4]), "depth" : 25 * mm});
        }
    });
